# Revit family: Innovo BEFR_IR 20 160 BEFR NAT
name_source: partatom
category: Mechanical Equipment
revit_build: Autodesk Revit 2015 (Build: 20160512_0715(x64)
units: mm (PartAtom-declared; Revit-internal decimal feet)

## types (1)
- IR-20-160 BEFR NAT
    1er Entretien (check-up) = 3 mois après l'installation
    2ème Entretien (Entretien Général) = 12 mois après l'installation
    Annual electricity consumption (1) = 37 kWh
    Annual electricity consumption (2) = -
    Annual fuel consumption (1) = 16 GJ GCV
    Annual fuel consumption (2) = -
    Assembly Code = D3010
    BIM Content Developer = CAD & Company
    CE-PIN = 0063CQ3037
    CO2 Émissions (tol. +/- 1.0) vol% = 9.3/7.5
    Capacité = 160.0 L
    Catégorie de Gaz = I2E(S)B
    Charge Maximale au Sol = 274 kg
    Charge Nominale (Valeur Inférieure) = 18000.0/14900.0
    Charge Nominale (Valeur Supérieure) = 20000.0/16600.0
    Class d'efficacité énergétique (1) = A
    Class d'efficacité énergétique (2) = -
    Consommation de Gaz - Masse kg/h = a/p
    Consommation de Gaz - Volume ltr/hr = 1.90/1.80
    D'autres profils de soutirage = -
    Description = Préparateur ECS Solaire en Combinaison avec Réservoir de Stockage
    Destination / Country = Belgique
    Diameter = 560 mm  [stored 1.83727 ft]
    Diamètre Cheminée - Boiler = 80/125 mm/mm
    Diamètre Cheminée - Système Concentrique = 80/125 mm/mm
    Diamètre Cheminée - Système Parallèle = 2x80
    Débit de vidage en Continu à ΔT = 28°C = 590.0 L/s
    Débit de vidage en Continu à ΔT = 44°C = 380.0 L/s
    Débit de vidage en Continu à ΔT = 50°C = 330.0 L/s
    Débit de vidage en Continu à ΔT = 55°C = 300.0 L/s
    Débit de vidage en Continu à ΔT = 70°C = 240.0 L/s
    Débit de vidage à ΔT = 28°C après 120 min. = 1500.0 L
    Débit de vidage à ΔT = 28°C après 30 min. = 530.0 L
    Débit de vidage à ΔT = 28°C après 60 min. = 820.0 L
    Débit de vidage à ΔT = 28°C après 90 min. = 1200.0 L
    Débit de vidage à ΔT = 44°C après 120 min. = 880.0 L
    Débit de vidage à ΔT = 44°C après 30 min. = 320.0 L
    Débit de vidage à ΔT = 44°C après 60 min. = 510.0 L
    Débit de vidage à ΔT = 44°C après 90 min. = 690.0 L
    Débit de vidage à ΔT = 50°C après 120 min. = 770.0 L
    Débit de vidage à ΔT = 50°C après 30 min. = 270.0 L
    Débit de vidage à ΔT = 50°C après 60 min. = 440.0 L
    Débit de vidage à ΔT = 50°C après 90 min. = 600.0 L
    Débit de vidage à ΔT = 55°C après 120 min. = 700.0 L
    Débit de vidage à ΔT = 55°C après 30 min. = 240.0 L
    Débit de vidage à ΔT = 55°C après 60 min. = 390.0 L
    Débit de vidage à ΔT = 55°C après 90 min. = 540.0 L
    Débit de vidage à ΔT = 70°C après 120 min. = 520.0 L
    Débit de vidage à ΔT = 70°C après 30 min. = 170.0 L
    Débit de vidage à ΔT = 70°C après 60 min. = 290.0 L
    Débit de vidage à ΔT = 70°C après 90 min. = 410.0 L
    Epaisseur d'Isolation = 50 mm  [stored 0.164042 ft]
    Fabricant No. = E 7110
    Forctionner qu'en heures creuses = No
    Fréquence secteur = 50 Hz
    Garantie Pièces = 12 mois
    Garantie sur la Cuve = 36 mois
    Hauteur = 1270 mm
    Hauteur Conduit d'Alimentation en Air = 1295 mm
    Hauteur Conduit d'Évacuation des Fumées = 1295 mm
    Hauteur d'emballage = 1465 mm
    Hauteur de l'Alimentation en eau Froide = 170 mm  [stored 0.557743 ft]
    Hauteur de la Sortie d'eau Chaude = 1270 mm
    Hauteur du Raccordement au Gaz = 860 mm
    L'efficacité énergétique pour le chauffage de l'eau (1) = 92%
    L'efficacité énergétique pour le chauffage de l'eau (2) = -
    La commande intelligente = No
    Largeur = 560 mm  [stored 1.83727 ft]
    Manufacturer = A.O. Smith Water Products Company b.v.
    Marque commerciale = A.O. Smith
    Model = IR-20-160 FR NAT
    Modèdele = IR-20-160
    NOx-émissions (ven air, 0% O2) ppm = 19.0/18.0
    NOx-émissions mg/kWh = 30.0/29.0
    Niveau de puissance acoustique à l'intérieur = 52 dB
    Niveau du Son dB (A) = <45
    Nombre de modèle du produit (EAN) = 8717449286019
    Pertes en Veille = 0 W
    Pertes en Veille - tous les jours (24h) = 0 W
    Phase = 1
    Poids de Transport = 114 kg
    Poids à vide = 95 kg
    Precaustions during assembling, installation or maintenance = voir Manuel d'installation, d'emploi er d'entretien
    Pression Amont de Gaz = 2000/2500 Pa
    Pression Différentielle d'Ouverture de l'Interrupteur de Pression < = 115.0 Pa
    Pression de Fonctionnement Maximale = 800000.0 Pa
    Production Nominale = 19100.0/15800.0
    Profils de soutirage déclaré = XL
    Profondeur = 780 mm  [stored 2.55906 ft]
    Profondeur d'emballage = 946 mm  [stored 3.10367 ft]
    Puissance Électrique Absorbée (nominal) = 36 W
    Puissance Électrique Absorbée (sommet) = 85 W
    Raccord Robinet de Vidange = 3/4"
    Raccord d'Alimentation en Eau Froide = 3/4"
    Raccord de Gaz = 15"
    Raccord de Sortie d'Eau Chaude = 3/4"
    Raccord de la Soupape de Vidange = 3/4"
    Raccord Évacuation de la Condensation = 40 mm  [stored 0.131234 ft]
    Rendement (Hi, acc. NEN-EN 89 - 1999) = 106
    Rendement (Hs, acc. NEN-EN 89 - 1999) = 95
    Rendement Saisonnier (Hs) = 95
    Réglage Standard Pour = G20/G25
    Réglages du thermostat du chauffe-eau = 65 °C
    Temps de réchauffement à ΔT = 28°C = 11
    Temps de réchauffement à ΔT = 44°C = 17
    Temps de réchauffement à ΔT = 50°C = 19
    Temps de réchauffement à ΔT = 55°C = 21
    Temps de réchauffement à ΔT = 70°C = 27
    Température Maximale des Fumées = 61 °C
    Tension d'Alimentation (-15%, +10%) = 230 V
    Type d'Installation = B23/C13/C33/C43/C53/C63
    Type d'emballage = Carton et bois
    URL = www.aosmith.be
    Valeur Défaut du Thermostat de Régulation = 65 °C
    Valeur Manimale du Thermostat de Régulation = 40 °C
    Valeur Maximale du Thermostat de Régulation = 85 °C
    Valve Height 01 = 604 mm  [stored 1.98163 ft]
    Valve Height 02 = 1070 mm  [stored 3.5105 ft]
    Workspace Front Distance = 1000 mm  [stored 3.28084 ft]
    Workspace Height = 2270 mm
    Workspace Radius = 730 mm  [stored 2.39501 ft]
    l'Intervalle d'Entretien = 12 mois
    largeur d'emballage = 786 mm  [stored 2.57874 ft]

note: [stored X ft] marks values corroborated as IEEE doubles in the binary element streams (Revit-internal decimal feet)

## geometry (parser evidence)
native form markers: Blend x26, Sweep x21
no freeform markers — native parametric forms only
